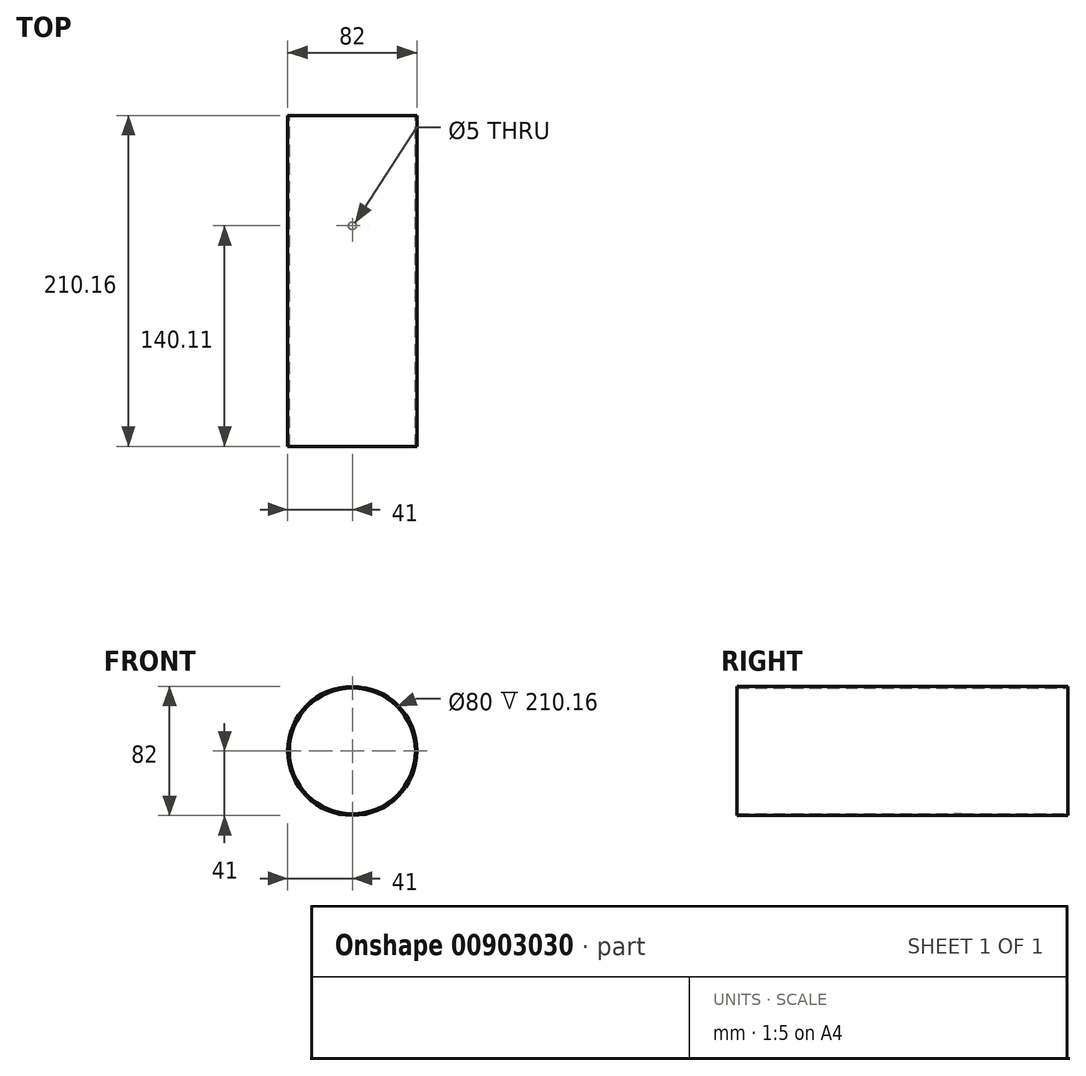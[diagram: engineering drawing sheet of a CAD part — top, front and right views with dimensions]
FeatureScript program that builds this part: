
annotation { "Feature Type Name" : "Feature", "Feature Type Description" : "" }
export const myFeature = defineFeature(function(context is Context, id is Id, definition is map)
    precondition{}
    {
        {
            assignVariable(context, id + "F0", {"name" : "diameter", "anyValue" : 80});
        }
        {
            assignVariable(context, id + "F1", {"name" : "wavelength", "anyValue" : 122.7});
        }
        {
            assignVariable(context, id + "F2", {"name" : "waveguide", "anyValue" : getVariable(context, 'wavelength') / sqrt(1 - (getVariable(context, 'wavelength') ^ 2 / (1.7 * getVariable(context, 'diameter')) ^ 2))});
        }
        {
            var Q0;
            Q0=qCreatedBy(makeId("Front.planeOp"),FACE);
            var sketch = newSketch(context, id + "F3", { "sketchPlane" : qUnion([Q0])});
            skCircle(sketch, "E0", {"center": v(0, 0) * mm, "radius": 40 * mm});
            skCircle(sketch, "E1", {"center": v(0, 0) * mm, "radius": 41 * mm});
            skSolve(sketch);
        }
        {
            var Q0;
            Q0=makeQuery(id+"F3.imprint","IMPRINT",FACE,{"disambiguationData":[TD([[makeQuery(id+"F3.imprint","IMPRINT",EDGE,{"derivedFrom":sQuery(id+"F3.wireOp",EDGE,"E0")}),-1.0]])]});
            extrude(context, id + "F4", {"entities" : qUnion([Q0]), "depth" : getVariable(context, 'waveguide') / 2 * mm, "offsetDistance" : 25 * mm, "hasSecondDirection" : true, "secondDirectionOppositeDirection" : true, "secondDirectionDepth" : getVariable(context, 'waveguide') / 4 * mm});
        }
        {
            var Q0;
            Q0=qCreatedBy(makeId("Top.planeOp"),FACE);
            var sketch = newSketch(context, id + "F5", { "sketchPlane" : qUnion([Q0])});
            skPoint(sketch, "E2", {"position": v(0, 0) * mm});
            skSolve(sketch);
        }
        {
            var Q0;
            Q0=sQuery(id+"F5.wireOp",VERTEX,"E2");
            var Q1;
            Q1=makeQuery(id+"F4.opExtrude","SWEPT_BODY",BODY,{"disambiguationData":[OSD([sQuery(id+"F3.wireOp",EDGE,"E0"),sQuery(id+"F3.wireOp",EDGE,"E1")])]});
            hole(context, id + "F6", {"style" : HoleStyle.SIMPLE, "endStyle" : HoleEndStyle.THROUGH, "holeDiameter" : 5 * mm, "majorDiameter" : 5 * mm, "isTappedThrough" : true, "tappedDepth" : 12 * mm, "tapClearance" : 3, "startFromSketch" : true, "locations" : qUnion([Q0]), "scope" : qUnion([Q1])});
        }
    });
